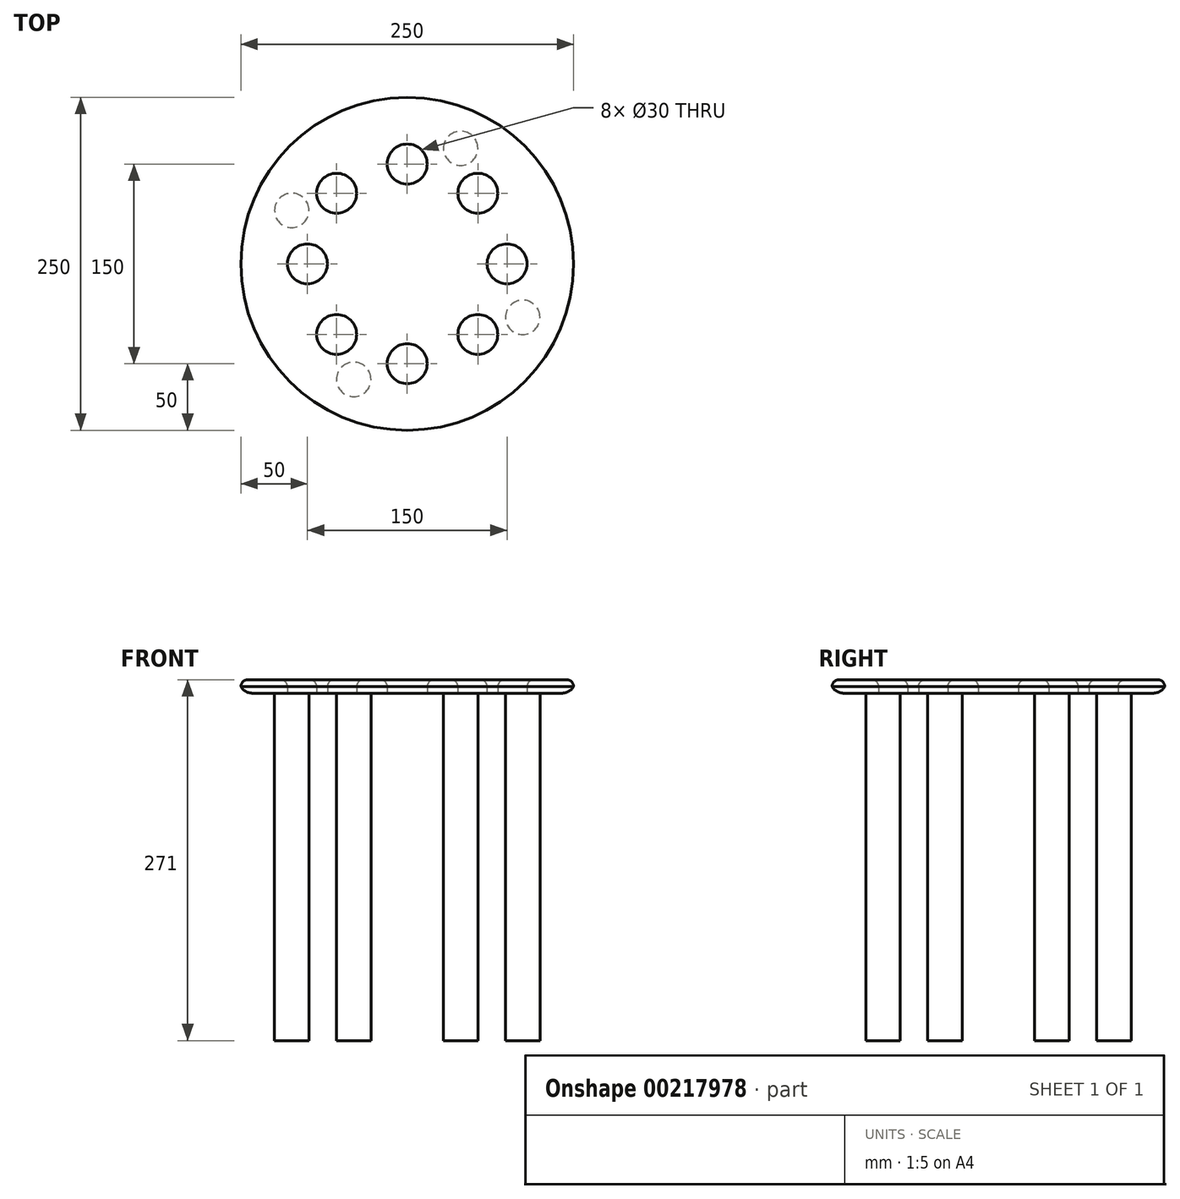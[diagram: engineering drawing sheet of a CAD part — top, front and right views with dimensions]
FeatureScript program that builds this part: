
annotation { "Feature Type Name" : "Feature", "Feature Type Description" : "" }
export const myFeature = defineFeature(function(context is Context, id is Id, definition is map)
    precondition{}
    {
        {
            var Q0;
            Q0=qCreatedBy(makeId("Top.planeOp"),FACE);
            var sketch = newSketch(context, id + "F0", { "sketchPlane" : qUnion([Q0])});
            skCircle(sketch, "E0", {"center": v(0, 0) * mm, "radius": 125 * mm});
            skSolve(sketch);
        }
        {
            var Q0;
            Q0=makeQuery(id+"F0.imprint","IMPRINT",FACE,{"disambiguationData":[TD([[makeQuery(id+"F0.imprint","IMPRINT",EDGE,{"derivedFrom":sQuery(id+"F0.wireOp",EDGE,"E0")}),1.0]])]});
            var sketch = newSketch(context, id + "F1", { "sketchPlane" : qUnion([Q0])});
            skCircle(sketch, "E1", {"center": v(0, 75) * mm, "radius": 15 * mm});
            skCircle(sketch, "E2.1.0", {"center": v(-53.03, 53.03) * mm, "radius": 15 * mm});
            skCircle(sketch, "E2.2.0", {"center": v(-75, 0) * mm, "radius": 15 * mm});
            skCircle(sketch, "E2.3.0", {"center": v(-53.03, -53.03) * mm, "radius": 15 * mm});
            skCircle(sketch, "E2.4.0", {"center": v(0, -75) * mm, "radius": 15 * mm});
            skCircle(sketch, "E2.5.0", {"center": v(53.03, -53.03) * mm, "radius": 15 * mm});
            skCircle(sketch, "E2.6.0", {"center": v(75, 0) * mm, "radius": 15 * mm});
            skCircle(sketch, "E2.7.0", {"center": v(53.03, 53.03) * mm, "radius": 15 * mm});
            skPoint(sketch, "E2.center", {"position": v(0, 0) * mm});
            skSolve(sketch);
        }
        {
            var Q0;
            Q0=makeQuery(id+"F1.imprint","IMPRINT",FACE,{"disambiguationData":[TD([[makeQuery(id+"F1.imprint","IMPRINT",EDGE,{"derivedFrom":sQuery(id+"F1.wireOp",EDGE,"E1")}),-1.0]])]});
            extrude(context, id + "F2", {"entities" : qUnion([Q0]), "depth" : 10 * mm});
        }
        {
            var Q0;
            Q0=makeQuery(id+"F2.opExtrude","CAP_FACE",FACE,{"disambiguationData":[OSD([sQuery(id+"F0.wireOp",EDGE,"E0"),sQuery(id+"F1.wireOp",EDGE,"E1"),sQuery(id+"F1.wireOp",EDGE,"E2.1.0"),sQuery(id+"F1.wireOp",EDGE,"E2.2.0"),sQuery(id+"F1.wireOp",EDGE,"E2.3.0"),sQuery(id+"F1.wireOp",EDGE,"E2.4.0"),sQuery(id+"F1.wireOp",EDGE,"E2.5.0"),sQuery(id+"F1.wireOp",EDGE,"E2.6.0"),sQuery(id+"F1.wireOp",EDGE,"E2.7.0")])],"isStart":false});
            fillet(context, id + "F3", {"entities" : qUnion([Q0]), "radius" : 5 * mm, "tangentPropagation" : true, "allowEdgeOverflow" : false});
        }
        {
            var Q0;
            {var subQ0=sQuery(id+"F0.wireOp",EDGE,"E0");Q0=makeQuery(id+"F3.opFillet","BLEND_EDGE",EDGE,{"blendedFrom":[makeQuery(id+"F2.opExtrude","CAP_EDGE",EDGE,{"disambiguationData":[OSD([subQ0])],"isStart":false}),makeQuery(id+"F2.opExtrude","CAP_FACE",FACE,{"disambiguationData":[OSD([subQ0,sQuery(id+"F1.wireOp",EDGE,"E1"),sQuery(id+"F1.wireOp",EDGE,"E2.1.0"),sQuery(id+"F1.wireOp",EDGE,"E2.2.0"),sQuery(id+"F1.wireOp",EDGE,"E2.3.0"),sQuery(id+"F1.wireOp",EDGE,"E2.4.0"),sQuery(id+"F1.wireOp",EDGE,"E2.5.0"),sQuery(id+"F1.wireOp",EDGE,"E2.6.0"),sQuery(id+"F1.wireOp",EDGE,"E2.7.0")])],"isStart":false})],"blendedInto":[makeQuery(id+"F2.opExtrude","CAP_FACE",FACE,{"disambiguationData":[OSD([subQ0,sQuery(id+"F1.wireOp",EDGE,"E1"),sQuery(id+"F1.wireOp",EDGE,"E2.1.0"),sQuery(id+"F1.wireOp",EDGE,"E2.2.0"),sQuery(id+"F1.wireOp",EDGE,"E2.3.0"),sQuery(id+"F1.wireOp",EDGE,"E2.4.0"),sQuery(id+"F1.wireOp",EDGE,"E2.5.0"),sQuery(id+"F1.wireOp",EDGE,"E2.6.0"),sQuery(id+"F1.wireOp",EDGE,"E2.7.0")])],"isStart":false})]});}
            var Q1;
            Q1=makeQuery(id+"F2.opExtrude","CAP_EDGE",EDGE,{"disambiguationData":[OSD([sQuery(id+"F0.wireOp",EDGE,"E0")])],"isStart":true});
            fillet(context, id + "F4", {"entities" : qUnion([Q0, Q1]), "radius" : 10 * mm, "tangentPropagation" : true, "allowEdgeOverflow" : false});
        }
        {
            var Q0;
            Q0=makeQuery(id+"F0.imprint","IMPRINT",FACE,{"disambiguationData":[TD([[makeQuery(id+"F0.imprint","IMPRINT",EDGE,{"derivedFrom":sQuery(id+"F0.wireOp",EDGE,"E0")}),1.0]])]});
            var sketch = newSketch(context, id + "F5", { "sketchPlane" : qUnion([Q0])});
            skCircle(sketch, "E3", {"center": v(40.16, 86.78) * mm, "radius": 12.92 * mm});
            skCircle(sketch, "E4.1.0", {"center": v(-86.78, 40.16) * mm, "radius": 12.92 * mm});
            skCircle(sketch, "E4.2.0", {"center": v(-40.16, -86.78) * mm, "radius": 12.92 * mm});
            skCircle(sketch, "E4.3.0", {"center": v(86.78, -40.16) * mm, "radius": 12.92 * mm});
            skPoint(sketch, "E4.center", {"position": v(0, 0) * mm});
            skSolve(sketch);
        }
        {
            var Q0;
            Q0 = qSketchRegion(id + "F5", true);
            extrude(context, id + "F6", {"entities" : qUnion([Q0]), "operationType" : NewBodyOperationType.ADD, "oppositeDirection" : true, "depth" : 261 * mm});
        }
    });
